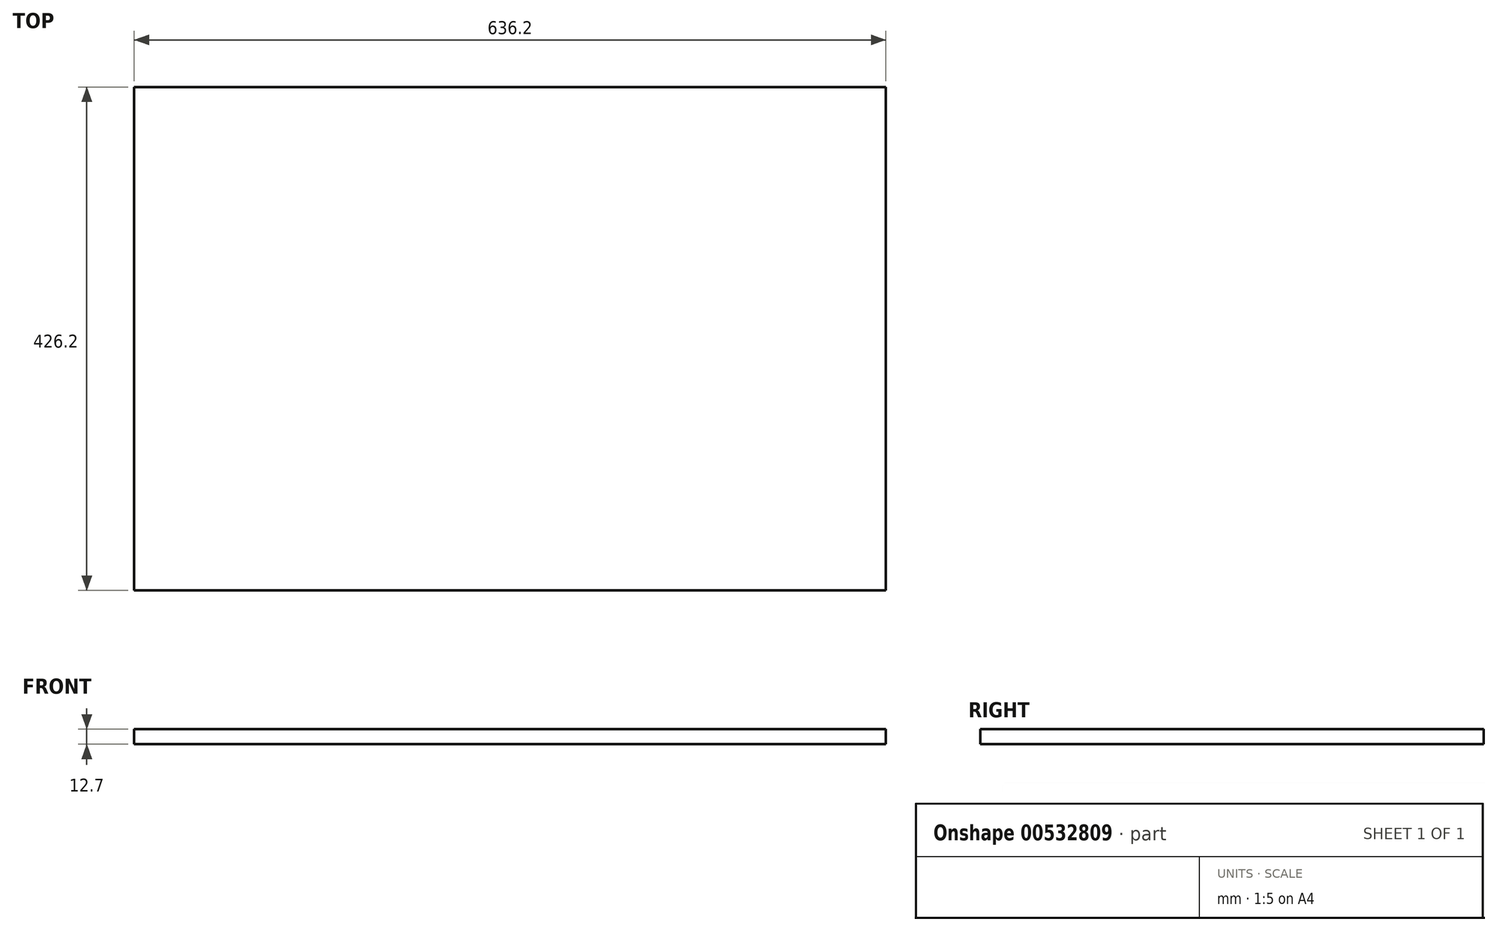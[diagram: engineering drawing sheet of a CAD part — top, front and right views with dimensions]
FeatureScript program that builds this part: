
annotation { "Feature Type Name" : "Feature", "Feature Type Description" : "" }
export const myFeature = defineFeature(function(context is Context, id is Id, definition is map)
    precondition{}
    {
        {
            var Q0;
            Q0=qCreatedBy(makeId("Top.planeOp"),FACE);
            var sketch = newSketch(context, id + "F0", { "sketchPlane" : qUnion([Q0])});
            skLineSegment(sketch, "E0.bottom", {"start": v(-318.1, 213.1) * mm, "end": v(318.1, 213.1) * mm});
            skLineSegment(sketch, "E0.top", {"start": v(-318.1, -213.1) * mm, "end": v(318.1, -213.1) * mm});
            skLineSegment(sketch, "E0.left", {"start": v(-318.1, 213.1) * mm, "end": v(-318.1, -213.1) * mm});
            skLineSegment(sketch, "E0.right", {"start": v(318.1, 213.1) * mm, "end": v(318.1, -213.1) * mm});
            skPoint(sketch, "E0.middle", {"position": v(0, 0) * mm});
            skSolve(sketch);
        }
        {
            var Q0;
            Q0=makeQuery(id+"F0.imprint","IMPRINT",FACE,{"disambiguationData":[TD([[makeQuery(id+"F0.imprint","IMPRINT",EDGE,{"derivedFrom":sQuery(id+"F0.wireOp",EDGE,"E0.bottom")}),-1.0]])]});
            extrude(context, id + "F1", {"entities" : qUnion([Q0]), "depth" : 12.7 * mm, "offsetDistance" : 25.4 * mm});
        }
    });
